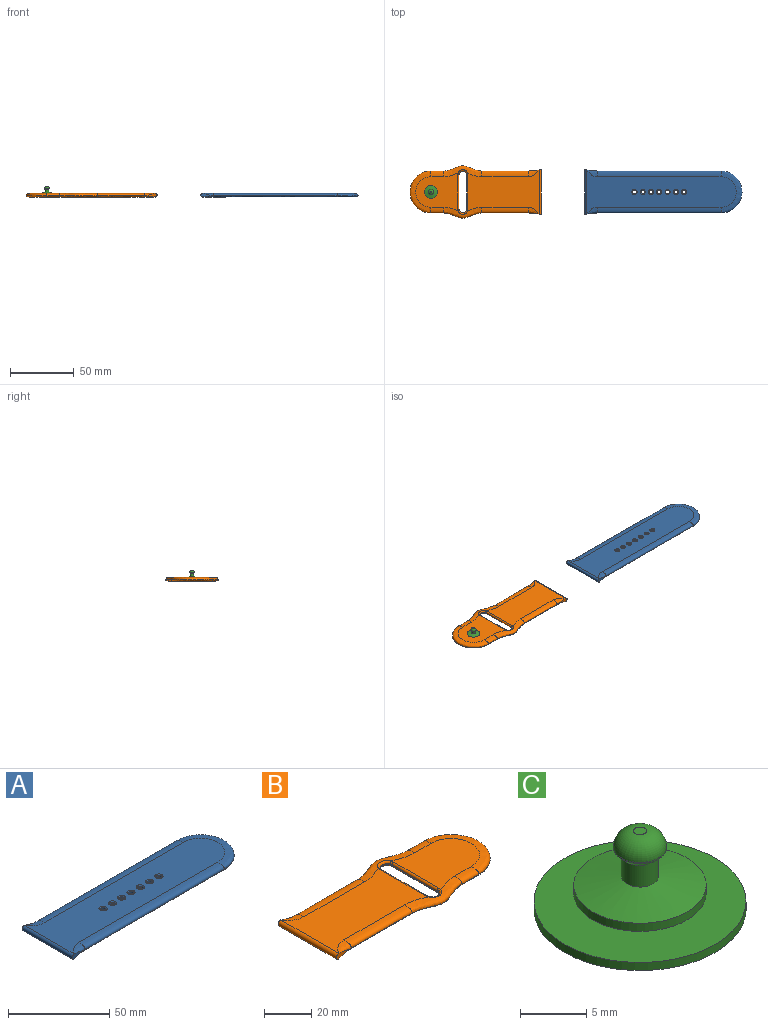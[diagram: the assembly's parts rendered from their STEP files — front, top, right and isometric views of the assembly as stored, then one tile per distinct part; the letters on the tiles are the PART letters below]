
ASSEMBLY  parts=3 mates=3
PART A: 43 faces, bbox 143.5x38.5x6.9 mm
  f0: plane 38.04x16.03mm, normal (0,0,-1), area 199.4mm2, adj f6,f7,f11,f13,f15,f17
  f1: plane 120.9x37.99mm, normal (0,0,1), area 2698mm2, adj f8,f9,f10,f11,f12,f14,f36,f37
  f2: extruded ~10x3mm, area 13.7mm2, adj f11,f12,f13
  f3: extruded ~10x3mm, area 13.7mm2, adj f11,f14,f15
  f4: plane 109.6x23.21mm, normal (0,0,-1), area 2338.2mm2, adj f16,f17,f18,f19,f20,f21,f29,f30
  f5: bspline ~33x33mm, area 115.5mm2, adj f6,f7,f9,f20
  f6: bspline ~97x3.5mm, area 239.2mm2, adj f0,f5,f10,f15,f16,f18
  f7: bspline ~97x3.5mm, area 239.2mm2, adj f0,f5,f8,f13,f19,f21
  f8: bspline ~97x4.5mm, area 538.1mm2, adj f1,f7,f9,f12
  f9: bspline ~33x33mm, area 255.1mm2, adj f1,f5,f8,f10
  f10: bspline ~97x4.5mm, area 538.1mm2, adj f1,f6,f9,f14
  f11: cylinder r=1.5mm len=35mm, axis (0,1,0), area 164mm2, adj f0,f1,f2,f3
  f12: bspline ~8.5x5.29mm, area 24.6mm2, adj f1,f2,f8
  f13: bspline ~8.5x4.29mm, area 13.4mm2, adj f0,f2,f7
  f14: bspline ~8.5x5.29mm, area 32.7mm2, adj f1,f3,f10
  f15: bspline ~8.5x4.29mm, area 17.7mm2, adj f0,f3,f6
  f16: bspline ~8.71x4.83mm, area 18.9mm2, adj f4,f6,f17,f18
  f17: torus R=11.5mm, axis (0,0,1), area 93.4mm2, adj f0,f4,f16,f19
  f18: cylinder r=5mm len=86.5mm, axis (-1,0,0), area 267.7mm2, adj f4,f6,f16,f20
  f19: bspline ~8.07x4.43mm, area 18.9mm2, adj f4,f7,f17,f21
  f20: torus R=11.6mm, axis (0,0,1), area 127.4mm2, adj f4,f5,f18,f21
  f21: cylinder r=5mm len=86.5mm, axis (1,0,0), area 267.7mm2, adj f4,f7,f19,f20
  f22: cylinder r=1.5mm len=3mm, axis (0,0,1), area 9.4mm2, adj f35,f36
  f23: cylinder r=1.5mm len=3mm, axis (0,0,1), area 9.4mm2, adj f34,f37
  f24: cylinder r=1.5mm len=3mm, axis (0,0,1), area 9.4mm2, adj f33,f38
  f25: cylinder r=1.5mm len=3mm, axis (0,0,1), area 9.4mm2, adj f32,f39
  f26: cylinder r=1.5mm len=3mm, axis (0,0,1), area 9.4mm2, adj f31,f40
  f27: cylinder r=1.5mm len=3mm, axis (0,0,1), area 9.4mm2, adj f30,f41
  f28: cylinder r=1.5mm len=3mm, axis (0,0,1), area 9.4mm2, adj f29,f42
  f29: torus R=2mm, axis (0,0,-1), area 8.3mm2, adj f4,f28
  f30: torus R=2mm, axis (0,0,-1), area 8.3mm2, adj f4,f27
  f31: torus R=2mm, axis (0,0,-1), area 8.3mm2, adj f4,f26
  f32: torus R=2mm, axis (0,0,-1), area 8.3mm2, adj f4,f25
  f33: torus R=2mm, axis (0,0,-1), area 8.3mm2, adj f4,f24
  f34: torus R=2mm, axis (0,0,-1), area 8.3mm2, adj f4,f23
  f35: torus R=2mm, axis (0,0,-1), area 8.3mm2, adj f4,f22
  f36: torus R=2mm, axis (0,0,1), area 8.3mm2, adj f1,f22
  f37: torus R=2mm, axis (0,0,1), area 8.3mm2, adj f1,f23
  f38: torus R=2mm, axis (0,0,1), area 8.3mm2, adj f1,f24
  f39: torus R=2mm, axis (0,0,1), area 8.3mm2, adj f1,f25
  f40: torus R=2mm, axis (0,0,1), area 8.3mm2, adj f1,f26
  f41: torus R=2mm, axis (0,0,1), area 8.3mm2, adj f1,f27
  f42: torus R=2mm, axis (0,0,1), area 8.3mm2, adj f1,f28
PART B: 50 faces, bbox 123x44.5x6.9 mm
  f0: plane 38.04x16.03mm, normal (0,0,-1), area 199.4mm2, adj f11,f18,f19,f32,f34,f36
  f1: plane 56.31x34.58mm, normal (0,0,1), area 1394.4mm2, adj f22,f23,f30,f31,f32,f33,f35,f42
  f2: plane 36.71x33.38mm, normal (0,0,1), area 752.8mm2, adj f23,f25,f27,f29,f30,f37,f38,f39
  f3: plane 33.56x31.52mm, normal (0,0,-1), area 804mm2, adj f14,f16,f17,f20,f21,f24,f26,f28
  f4: cylinder r=3mm len=5.93mm, axis (0,0,-1), area 2.3mm2, adj f5,f38,f40,f43,f45,f47
  f5: plane 27x0.34mm, normal (-1,0,0), area 9.3mm2, adj f4,f6,f37,f49
  f6: cylinder r=3mm len=5.93mm, axis (0,0,-1), area 2.3mm2, adj f5,f39,f41,f44,f46,f48
  f7: extruded ~10x3mm, area 13.7mm2, adj f32,f35,f36
  f8: extruded ~10x3mm, area 13.7mm2, adj f32,f33,f34
  f9: plane 48.6x28.69mm, normal (0,0,-1), area 1080.7mm2, adj f10,f11,f12,f13,f15,f42,f43,f44
  f10: cylinder r=5mm len=26mm, axis (-1,0,0), area 80.9mm2, adj f9,f11,f12,f18
  f11: torus R=11.5mm, axis (0,0,1), area 131.2mm2, adj f0,f9,f10,f13,f18,f19
  f12: bspline ~15.45x7mm, area 44.8mm2, adj f9,f10,f14,f20,f46
  f13: cylinder r=5mm len=26mm, axis (-1,0,0), area 80.9mm2, adj f9,f11,f15,f19
  f14: torus R=2mm, axis (0,0,1), area 10.1mm2, adj f3,f12,f16,f20,f48
  f15: bspline ~15.45x7mm, area 44.8mm2, adj f9,f13,f17,f21,f45
  f16: cylinder r=5mm len=27mm, axis (0,1,0), area 41mm2, adj f3,f14,f17,f49
  f17: torus R=2mm, axis (0,0,1), area 10.1mm2, adj f3,f15,f16,f21,f47
  f18: bspline ~36.5x3.5mm, area 99.3mm2, adj f0,f10,f11,f20,f22,f34
  f19: bspline ~36.5x3.5mm, area 99.3mm2, adj f0,f11,f13,f21,f31,f36
  f20: bspline ~30x7.5mm, area 95.2mm2, adj f3,f12,f14,f18,f23,f24
  f21: bspline ~30x7.5mm, area 95.2mm2, adj f3,f15,f17,f19,f28,f30
  f22: bspline ~36.5x4.5mm, area 202.5mm2, adj f1,f18,f23,f33
  f23: bspline ~30x8.5mm, area 173.4mm2, adj f1,f2,f20,f22,f25,f41
  f24: bspline ~10x3.5mm, area 38.6mm2, adj f3,f20,f25,f26
  f25: bspline ~10x4.5mm, area 55.5mm2, adj f2,f23,f24,f27
  f26: bspline ~33x33mm, area 180.4mm2, adj f3,f24,f27,f28
  f27: bspline ~33x33mm, area 255.1mm2, adj f2,f25,f26,f29
  f28: bspline ~10x3.5mm, area 38.6mm2, adj f3,f21,f26,f29
  f29: bspline ~10x4.5mm, area 55.5mm2, adj f2,f27,f28,f30
  f30: bspline ~30x8.5mm, area 173.4mm2, adj f1,f2,f21,f29,f31,f40
  f31: bspline ~36.5x4.5mm, area 202.5mm2, adj f1,f19,f30,f35
  f32: cylinder r=1.5mm len=35mm, axis (0,1,0), area 164mm2, adj f0,f1,f7,f8
  f33: bspline ~8.5x5.29mm, area 32.7mm2, adj f1,f8,f22
  f34: bspline ~8.5x4.29mm, area 13.4mm2, adj f0,f8,f18
  f35: bspline ~8.5x5.29mm, area 32.7mm2, adj f1,f7,f31
  f36: bspline ~8.5x4.29mm, area 13.4mm2, adj f0,f7,f19
  f37: cylinder r=1mm len=27mm, axis (0,1,0), area 42.4mm2, adj f2,f5,f38,f39
  f38: torus R=4mm, axis (0,0,1), area 2mm2, adj f2,f4,f37,f40
  f39: torus R=4mm, axis (0,0,1), area 2mm2, adj f2,f6,f37,f41
  f40: bspline ~7.64x3.31mm, area 13.1mm2, adj f4,f30,f38,f43
  f41: bspline ~7.64x3.31mm, area 13.1mm2, adj f6,f23,f39,f44
  f42: cylinder r=1mm len=27mm, axis (0,-1,0), area 84.8mm2, adj f1,f9,f43,f44
  f43: torus R=4mm, axis (0,0,1), area 3.1mm2, adj f1,f4,f9,f40,f42,f45
  f44: torus R=4mm, axis (0,0,1), area 3.1mm2, adj f1,f6,f9,f41,f42,f46
  f45: bspline ~4.88x3.62mm, area 6mm2, adj f4,f15,f43,f47
  f46: bspline ~4.88x3.62mm, area 6mm2, adj f6,f12,f44,f48
  f47: torus R=4mm, axis (0,0,1), area 6.3mm2, adj f4,f17,f45,f49
  f48: torus R=4mm, axis (0,0,1), area 6.3mm2, adj f6,f14,f46,f49
  f49: cylinder r=1mm len=27mm, axis (0,1,0), area 33.2mm2, adj f5,f16,f47,f48
PART C: 14 faces, bbox 16x16x8 mm
  f0: plane 10x10mm, normal (0,0,-1), area 78.5mm2, adj f12
  f1: plane 1x1mm, normal (0,0,1), area 0.8mm2, adj f13
  f2: cylinder r=2mm len=4mm, axis (0,0,-1), area 1.3mm2, adj f3,f13
  f3: cone r=1.4mm half-angle=45deg, axis (0,0,1), area 9.1mm2, adj f2,f4
  f4: cylinder r=1.4mm len=2.8mm, axis (0,0,-1), area 17.6mm2, adj f3,f5
  f5: cone r=5mm half-angle=77.5deg, axis (0,0,-1), area 74.1mm2, adj f4,f6
  f6: cylinder r=5mm len=10mm, axis (0,0,-1), area 23.6mm2, adj f5,f7
  f7: plane 10x10mm, normal (0,0,-1), area 58.9mm2, adj f6,f8
  f8: cylinder r=2.5mm len=5mm, axis (0,0,-1), area 11.8mm2, adj f7,f9
  f9: plane 16x16mm, normal (0,0,1), area 181.4mm2, adj f8,f10
  f10: cylinder r=8mm len=16mm, axis (0,0,-1), area 37.7mm2, adj f9,f11
  f11: plane 16x16mm, normal (0,0,-1), area 122.5mm2, adj f10,f12
  f12: cylinder r=5mm len=10mm, axis (0,0,-1), area 23.6mm2, adj f0,f11
  f13: torus R=0.5mm, axis (0,0,1), area 21.5mm2, adj f1,f2
PLACE A t=(183.98,51.3,23.36)mm
PLACE B rot(axis=(0,0,1),180deg) t=(-43.93,51.3,23.36)mm
PLACE C t=(-43.93,51.3,23.36)mm
MATE revolute B.f3 <-> C.f2  axis (0,0,-1) through (-43.93,51.3,23.36)mm
MATE planar B.f37 <-> A.f11  axis (0,-1,0) through (-22.93,51.3,25.36)mm
MATE planar B.f1 <-> A.f1  axis (0,0,1) through (13.18,51.3,26.36)mm
